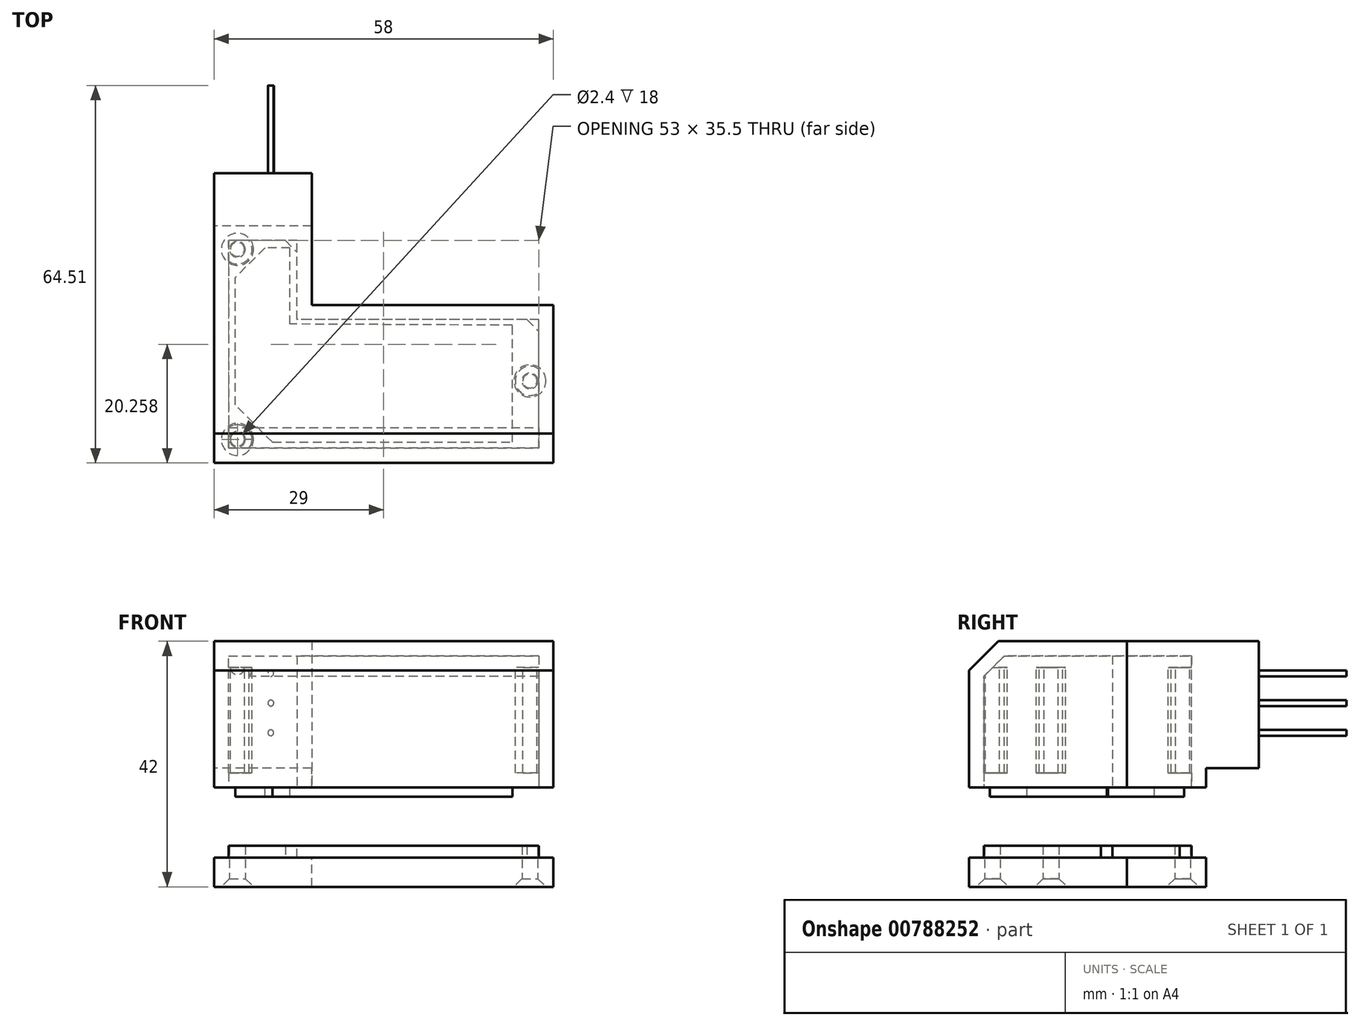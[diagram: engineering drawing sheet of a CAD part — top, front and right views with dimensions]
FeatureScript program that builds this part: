
annotation { "Feature Type Name" : "Feature", "Feature Type Description" : "" }
export const myFeature = defineFeature(function(context is Context, id is Id, definition is map)
    precondition{}
    {
        {
            var Q0;
            Q0=qCreatedBy(makeId("Top.planeOp"),FACE);
            var sketch = newSketch(context, id + "F0", { "sketchPlane" : qUnion([Q0])});
            skLineSegment(sketch, "E0", {"start": v(-27.66, 15.13) * mm, "end": v(-27.66, -18.85) * mm});
            skLineSegment(sketch, "E1", {"start": v(-27.66, -18.85) * mm, "end": v(30.34, -18.85) * mm});
            skLineSegment(sketch, "E2", {"start": v(30.34, -18.85) * mm, "end": v(30.34, 8.15) * mm});
            skLineSegment(sketch, "E3", {"start": v(30.34, 8.15) * mm, "end": v(-10.96, 8.15) * mm});
            skLineSegment(sketch, "E4", {"start": v(-10.96, 8.15) * mm, "end": v(-10.96, 30.65) * mm});
            skLineSegment(sketch, "E5", {"start": v(-10.96, 30.65) * mm, "end": v(-27.66, 30.65) * mm});
            skLineSegment(sketch, "E6", {"start": v(-27.66, 30.65) * mm, "end": v(-27.66, 15.13) * mm});
            skSolve(sketch);
        }
        {
            var Q0;
            Q0=makeQuery(id+"F0.imprint","IMPRINT",FACE,{"disambiguationData":[TD([[makeQuery(id+"F0.imprint","IMPRINT",EDGE,{"derivedFrom":sQuery(id+"F0.wireOp",EDGE,"E0")}),1.0]])]});
            extrude(context, id + "F1", {"entities" : qUnion([Q0]), "depth" : 25 * mm, "offsetDistance" : 25 * mm});
        }
        {
            var Q0;
            Q0=makeQuery(id+"F1.opExtrude","SWEPT_FACE",FACE,{"disambiguationData":[OSD([sQuery(id+"F0.wireOp",EDGE,"E0"),sQuery(id+"F0.wireOp",EDGE,"E6")])]});
            var sketch = newSketch(context, id + "F2", { "sketchPlane" : qUnion([Q0])});
            skLineSegment(sketch, "E7", {"start": v(-30.65, 3.3) * mm, "end": v(-21.65, 3.3) * mm});
            skLineSegment(sketch, "E8", {"start": v(-21.65, 3.3) * mm, "end": v(-21.65, 0) * mm});
            skSolve(sketch);
        }
        {
            var Q0;
            {var subQ0=sQuery(id+"F2.wireOp",EDGE,"E7");Q0=makeQuery(id+"F2.imprint","IMPRINT",FACE,{"disambiguationData":[TD([[makeQuery(id+"F2.imprint","IMPRINT",EDGE,{"derivedFrom":subQ0}),-1.0]])]});}
            var Q1;
            Q1=makeQuery(id+"F1.opExtrude","SWEPT_FACE",FACE,{"disambiguationData":[OSD([sQuery(id+"F0.wireOp",EDGE,"E4")])]});
            extrude(context, id + "F3", {"entities" : qUnion([Q0]), "operationType" : NewBodyOperationType.REMOVE, "endBound" : BoundingType.UP_TO_SURFACE, "oppositeDirection" : true, "depth" : 25 * mm, "endBoundEntityFace" : qUnion([Q1]), "offsetDistance" : 25 * mm});
        }
        {
            var Q0;
            Q0=makeQuery(id+"F1.opExtrude","CAP_EDGE",EDGE,{"disambiguationData":[OSD([sQuery(id+"F0.wireOp",EDGE,"E1")])],"isStart":false});
            chamfer(context, id + "F4", {"entities" : qUnion([Q0]), "width" : 5 * mm, "tangentPropagation" : true});
        }
        {
            var Q0;
            Q0=makeQuery(id+"F1.opExtrude","SWEPT_FACE",FACE,{"disambiguationData":[OSD([sQuery(id+"F0.wireOp",EDGE,"E5")])]});
            var sketch = newSketch(context, id + "F5", { "sketchPlane" : qUnion([Q0])});
            skLineSegment(sketch, "E9", {"start": v(17.96, 25) * mm, "end": v(17.96, 3.3) * mm, "construction": true});
            skCircle(sketch, "E10", {"center": v(17.96, 19.5) * mm, "radius": 0.5 * mm});
            skCircle(sketch, "E11", {"center": v(17.94, 14.42) * mm, "radius": 0.5 * mm});
            skCircle(sketch, "E12", {"center": v(17.96, 9.34) * mm, "radius": 0.5 * mm});
            skSolve(sketch);
        }
        {
            var Q0;
            Q0=makeQuery(id+"F5.imprint","IMPRINT",FACE,{"disambiguationData":[TD([[makeQuery(id+"F5.imprint","IMPRINT",EDGE,{"derivedFrom":sQuery(id+"F5.wireOp",EDGE,"E10")}),1.0]])]});
            var Q1;
            Q1=makeQuery(id+"F5.imprint","IMPRINT",FACE,{"disambiguationData":[TD([[makeQuery(id+"F5.imprint","IMPRINT",EDGE,{"derivedFrom":sQuery(id+"F5.wireOp",EDGE,"E11")}),1.0]])]});
            var Q2;
            Q2=makeQuery(id+"F5.imprint","IMPRINT",FACE,{"disambiguationData":[TD([[makeQuery(id+"F5.imprint","IMPRINT",EDGE,{"derivedFrom":sQuery(id+"F5.wireOp",EDGE,"E12")}),1.0]])]});
            extrude(context, id + "F6", {"entities" : qUnion([Q0, Q1, Q2]), "operationType" : NewBodyOperationType.ADD, "depth" : 15 * mm, "offsetDistance" : 25 * mm});
        }
        {
            var Q0;
            Q0=makeQuery(id+"F1.opExtrude","CAP_FACE",FACE,{"disambiguationData":[OSD([sQuery(id+"F0.wireOp",EDGE,"E0"),sQuery(id+"F0.wireOp",EDGE,"E1"),sQuery(id+"F0.wireOp",EDGE,"E2"),sQuery(id+"F0.wireOp",EDGE,"E3"),sQuery(id+"F0.wireOp",EDGE,"E4"),sQuery(id+"F0.wireOp",EDGE,"E5"),sQuery(id+"F0.wireOp",EDGE,"E6")])],"isStart":true});
            shell(context, id + "F7", {"entities" : qUnion([Q0]), "thickness" : 2.5 * mm});
        }
        {
            var Q0;
            Q0=makeQuery(id+"F7.opShell","OFFSET_FACE",FACE,{"disambiguationData":[OSD([sQuery(id+"F0.wireOp",EDGE,"E5")])]});
            var Q1;
            Q1=makeQuery(id+"F7.opShell","OFFSET_FACE",FACE,{"disambiguationData":[OSD([sQuery(id+"F2.wireOp",EDGE,"E8")])]});
            extrude(context, id + "F8", {"entities" : qUnion([Q0]), "operationType" : NewBodyOperationType.ADD, "endBound" : BoundingType.UP_TO_SURFACE, "depth" : 25 * mm, "endBoundEntityFace" : qUnion([Q1]), "offsetDistance" : 25 * mm});
        }
        {
            var Q0;
            Q0=makeQuery(id+"F1.opExtrude","CAP_FACE",FACE,{"disambiguationData":[OSD([sQuery(id+"F0.wireOp",EDGE,"E0"),sQuery(id+"F0.wireOp",EDGE,"E1"),sQuery(id+"F0.wireOp",EDGE,"E2"),sQuery(id+"F0.wireOp",EDGE,"E3"),sQuery(id+"F0.wireOp",EDGE,"E4"),sQuery(id+"F0.wireOp",EDGE,"E5"),sQuery(id+"F0.wireOp",EDGE,"E6")])],"isStart":true});
            cPlane(context, id + "F9", {"entities" : qUnion([Q0]), "cplaneType" : CPlaneType.OFFSET, "offset" : 10 * mm, "width" : 150 * mm, "height" : 150 * mm});
        }
        {
            var Q0;
            Q0=qCreatedBy(id+"F9.planeOp",FACE);
            var sketch = newSketch(context, id + "F10", { "sketchPlane" : qUnion([Q0])});
            skLineSegment(sketch, "E13", {"start": v(-25.16, 16.35) * mm, "end": v(27.84, 16.35) * mm});
            skLineSegment(sketch, "E14", {"start": v(27.84, 16.35) * mm, "end": v(27.84, -5.65) * mm});
            skLineSegment(sketch, "E15", {"start": v(27.84, -5.65) * mm, "end": v(-13.46, -5.65) * mm});
            skLineSegment(sketch, "E16", {"start": v(-13.46, -5.65) * mm, "end": v(-13.46, -19.15) * mm});
            skLineSegment(sketch, "E17", {"start": v(-13.46, -19.15) * mm, "end": v(-25.16, -19.15) * mm});
            skLineSegment(sketch, "E18", {"start": v(-25.16, 16.35) * mm, "end": v(-25.16, -19.15) * mm});
            skSolve(sketch);
        }
        {
            var Q0;
            {var subQ2=sQuery(id+"F10.wireOp",EDGE,"E13");Q0=makeQuery(id+"F10.imprint","IMPRINT",FACE,{"disambiguationData":[TD([[makeQuery(id+"F10.imprint","IMPRINT",EDGE,{"derivedFrom":subQ2}),-1.0]])]});}
            extrude(context, id + "F11", {"entities" : qUnion([Q0]), "depth" : 2 * mm, "offsetDistance" : 25 * mm});
        }
        {
            var Q0;
            Q0=makeQuery(id+"F11.opExtrude","CAP_FACE",FACE,{"disambiguationData":[OSD([sQuery(id+"F10.wireOp",EDGE,"E13"),sQuery(id+"F10.wireOp",EDGE,"ugxWyxvC-Y8jT-QxUj-v6cB-LJvaZN0y2NzD"),sQuery(id+"F10.wireOp",EDGE,"E14"),sQuery(id+"F10.wireOp",EDGE,"E15"),sQuery(id+"F10.wireOp",EDGE,"E16"),sQuery(id+"F10.wireOp",EDGE,"E17"),sQuery(id+"F10.wireOp",EDGE,"E18")])],"isStart":false});
            var sketch = newSketch(context, id + "F12", { "sketchPlane" : qUnion([Q0])});
            skLineSegment(sketch, "E19", {"start": v(-27.66, -21.65) * mm, "end": v(-10.96, -21.65) * mm});
            skLineSegment(sketch, "E20", {"start": v(-10.96, -21.65) * mm, "end": v(-10.96, -8.15) * mm});
            skLineSegment(sketch, "E21", {"start": v(-10.96, -8.15) * mm, "end": v(30.34, -8.15) * mm});
            skLineSegment(sketch, "E22", {"start": v(30.34, -8.15) * mm, "end": v(30.34, 18.86) * mm});
            skLineSegment(sketch, "E23", {"start": v(30.34, 18.86) * mm, "end": v(28.63, 18.85) * mm});
            skLineSegment(sketch, "E24", {"start": v(28.63, 18.85) * mm, "end": v(-27.66, 18.85) * mm});
            skLineSegment(sketch, "E25", {"start": v(-27.66, 18.85) * mm, "end": v(-27.66, -21.65) * mm});
            skSolve(sketch);
        }
        {
            var Q0;
            Q0=makeQuery(id+"F12.imprint","IMPRINT",FACE,{"disambiguationData":[TD([[makeQuery(id+"F12.imprint","IMPRINT",EDGE,{"derivedFrom":makeQuery(id+"F11.opExtrude","CAP_EDGE",EDGE,{"disambiguationData":[OSD([sQuery(id+"F10.wireOp",EDGE,"E13")])],"isStart":false})}),-1.0]])]});
            var Q1;
            Q1=makeQuery(id+"F12.imprint","IMPRINT",FACE,{"disambiguationData":[TD([[makeQuery(id+"F12.imprint","IMPRINT",EDGE,{"derivedFrom":sQuery(id+"F12.wireOp",EDGE,"E19")}),1.0]])]});
            extrude(context, id + "F13", {"entities" : qUnion([Q0, Q1]), "operationType" : NewBodyOperationType.ADD, "depth" : 5 * mm, "offsetDistance" : 25 * mm});
        }
        {
            var Q0;
            Q0=makeQuery(id+"F13.opExtrude","CAP_FACE",FACE,{"disambiguationData":[OSD([sQuery(id+"F12.wireOp",EDGE,"E19"),sQuery(id+"F12.wireOp",EDGE,"E20"),sQuery(id+"F12.wireOp",EDGE,"E21"),sQuery(id+"F12.wireOp",EDGE,"E22"),sQuery(id+"F12.wireOp",EDGE,"E23"),sQuery(id+"F12.wireOp",EDGE,"E24"),sQuery(id+"F12.wireOp",EDGE,"E25")])],"isStart":false});
            var sketch = newSketch(context, id + "F14", { "sketchPlane" : qUnion([Q0])});
            skPoint(sketch, "E26", {"position": v(-23.66, 14.85) * mm});
            skPoint(sketch, "E27", {"position": v(-23.66, -17.65) * mm});
            skLineSegment(sketch, "E28", {"start": v(-29.6, 4.85) * mm, "end": v(35.29, 4.85) * mm, "construction": true});
            skLineSegment(sketch, "E29", {"start": v(-23.66, 21.05) * mm, "end": v(-23.66, -24.23) * mm, "construction": true});
            skPoint(sketch, "E30", {"position": v(26.34, 4.85) * mm});
            skSolve(sketch);
        }
        {
            var Q0;
            Q0=sQuery(id+"F14.wireOp",VERTEX,"E27");
            var Q1;
            Q1=sQuery(id+"F14.wireOp",VERTEX,"E26");
            var Q2;
            Q2=sQuery(id+"F14.wireOp",VERTEX,"E30");
            var Q3;
            Q3=makeQuery(id+"F1.opExtrude","SWEPT_BODY",BODY,{"disambiguationData":[OSD([sQuery(id+"F0.wireOp",EDGE,"E0"),sQuery(id+"F0.wireOp",EDGE,"E1"),sQuery(id+"F0.wireOp",EDGE,"E2"),sQuery(id+"F0.wireOp",EDGE,"E3"),sQuery(id+"F0.wireOp",EDGE,"E4"),sQuery(id+"F0.wireOp",EDGE,"E5"),sQuery(id+"F0.wireOp",EDGE,"E6")])]});
            var Q4;
            Q4=makeQuery(id+"F11.opExtrude","SWEPT_BODY",BODY,{"disambiguationData":[OSD([sQuery(id+"F10.wireOp",EDGE,"E13"),sQuery(id+"F10.wireOp",EDGE,"ugxWyxvC-Y8jT-QxUj-v6cB-LJvaZN0y2NzD"),sQuery(id+"F10.wireOp",EDGE,"E14"),sQuery(id+"F10.wireOp",EDGE,"E15"),sQuery(id+"F10.wireOp",EDGE,"E16"),sQuery(id+"F10.wireOp",EDGE,"E17"),sQuery(id+"F10.wireOp",EDGE,"E18")])]});
            hole(context, id + "F15", {"style" : HoleStyle.C_SINK, "endStyle" : HoleEndStyle.BLIND, "holeDiameter" : 2.7 * mm, "cSinkDiameter" : 5.5 * mm, "cSinkAngle" : 90 * degree, "majorDiameter" : 5 * mm, "holeDepth" : 7 * mm, "isTappedThrough" : true, "tappedDepth" : 12 * mm, "tapClearance" : 3, "locations" : qUnion([Q0, Q1, Q2]), "scope" : qUnion([Q3, Q4])});
        }
        {
            var Q0;
            Q0=makeQuery(id+"F7.opShell","OFFSET_FACE",FACE,{"disambiguationData":[OSD([sQuery(id+"F0.wireOp",EDGE,"E0"),sQuery(id+"F0.wireOp",EDGE,"E1"),sQuery(id+"F0.wireOp",EDGE,"E2"),sQuery(id+"F0.wireOp",EDGE,"E3"),sQuery(id+"F0.wireOp",EDGE,"E4"),sQuery(id+"F0.wireOp",EDGE,"E5"),sQuery(id+"F0.wireOp",EDGE,"E6")])]});
            var Q1;
            Q1 = qBodyType(qCreatedBy(id + "F17" ,EDGE), BodyType.WIRE);
            cPlane(context, id + "F16", {"entities" : qUnion([Q0, Q1]), "cplaneType" : CPlaneType.OFFSET, "offset" : 2 * mm, "width" : 150 * mm, "height" : 150 * mm});
        }
        {
            var Q0;
            Q0=qCreatedBy(id+"F16.planeOp",FACE);
            var sketch = newSketch(context, id + "F17", { "sketchPlane" : qUnion([Q0])});
            skPoint(sketch, "E31", {"position": v(-23.66, -17.65) * mm});
            skPoint(sketch, "E32", {"position": v(26.34, 4.85) * mm});
            skPoint(sketch, "E33", {"position": v(-23.66, 14.85) * mm});
            skCircle(sketch, "E34", {"center": v(-23.66, 14.85) * mm, "radius": 2.5 * mm});
            skCircle(sketch, "E35", {"center": v(-23.66, -17.65) * mm, "radius": 2.5 * mm});
            skCircle(sketch, "E36", {"center": v(26.34, 4.85) * mm, "radius": 2.5 * mm});
            skCircle(sketch, "E37", {"center": v(-23.66, 14.85) * mm, "radius": 1.2 * mm});
            skCircle(sketch, "E38", {"center": v(-23.66, -17.65) * mm, "radius": 1.2 * mm});
            skCircle(sketch, "E39", {"center": v(26.34, 4.85) * mm, "radius": 1.2 * mm});
            skSolve(sketch);
        }
        {
            var Q0;
            Q0=makeQuery(id+"F17.imprint","IMPRINT",FACE,{"disambiguationData":[TD([[makeQuery(id+"F17.imprint","IMPRINT",EDGE,{"derivedFrom":sQuery(id+"F17.wireOp",EDGE,"E38")}),-1.0]])]});
            var Q1;
            Q1=makeQuery(id+"F17.imprint","IMPRINT",FACE,{"disambiguationData":[TD([[makeQuery(id+"F17.imprint","IMPRINT",EDGE,{"derivedFrom":sQuery(id+"F17.wireOp",EDGE,"E37")}),-1.0]])]});
            var Q2;
            Q2=makeQuery(id+"F17.imprint","IMPRINT",FACE,{"disambiguationData":[TD([[makeQuery(id+"F17.imprint","IMPRINT",EDGE,{"derivedFrom":sQuery(id+"F17.wireOp",EDGE,"E39")}),-1.0]])]});
            var Q3;
            Q3=makeQuery(id+"F1.opExtrude","CAP_FACE",FACE,{"disambiguationData":[OSD([sQuery(id+"F0.wireOp",EDGE,"E0"),sQuery(id+"F0.wireOp",EDGE,"E1"),sQuery(id+"F0.wireOp",EDGE,"E2"),sQuery(id+"F0.wireOp",EDGE,"E3"),sQuery(id+"F0.wireOp",EDGE,"E4"),sQuery(id+"F0.wireOp",EDGE,"E5"),sQuery(id+"F0.wireOp",EDGE,"E6")])],"isStart":true});
            extrude(context, id + "F18", {"entities" : qUnion([Q0, Q1, Q2]), "operationType" : NewBodyOperationType.ADD, "depth" : 18 * mm, "endBoundEntityFace" : qUnion([Q3]), "offsetDistance" : 25 * mm});
        }
        {
            var Q0;
            Q0=makeQuery(id+"F11.opExtrude","SWEPT_EDGE",EDGE,{"disambiguationData":[OSD([sQuery(id+"F10.wireOp",EDGE,"E16"),sQuery(id+"F10.wireOp",EDGE,"E17")])]});
            var Q1;
            Q1=makeQuery(id+"F11.opExtrude","SWEPT_EDGE",EDGE,{"disambiguationData":[OSD([sQuery(id+"F10.wireOp",EDGE,"E14"),sQuery(id+"F10.wireOp",EDGE,"E15")])]});
            chamfer(context, id + "F19", {"entities" : qUnion([Q0, Q1]), "width" : 2 * mm, "tangentPropagation" : true});
        }
        {
            var Q0;
            Q0=makeQuery(id+"F1.opExtrude","CAP_FACE",FACE,{"disambiguationData":[OSD([sQuery(id+"F0.wireOp",EDGE,"E0"),sQuery(id+"F0.wireOp",EDGE,"E1"),sQuery(id+"F0.wireOp",EDGE,"E2"),sQuery(id+"F0.wireOp",EDGE,"E3"),sQuery(id+"F0.wireOp",EDGE,"E4"),sQuery(id+"F0.wireOp",EDGE,"E5"),sQuery(id+"F0.wireOp",EDGE,"E6")])],"isStart":true});
            var sketch = newSketch(context, id + "F20", { "sketchPlane" : qUnion([Q0])});
            skLineSegment(sketch, "E40", {"start": v(-17.66, 15.33) * mm, "end": v(23.34, 15.33) * mm});
            skLineSegment(sketch, "E41", {"start": v(23.34, 15.33) * mm, "end": v(23.34, -4.67) * mm});
            skLineSegment(sketch, "E42", {"start": v(23.34, -4.67) * mm, "end": v(-14.66, -4.86) * mm});
            skLineSegment(sketch, "E43", {"start": v(-14.66, -4.86) * mm, "end": v(-14.66, -17.88) * mm});
            skLineSegment(sketch, "E44", {"start": v(-14.66, -17.88) * mm, "end": v(-18.96, -17.88) * mm});
            skLineSegment(sketch, "E45", {"start": v(-18.96, -17.88) * mm, "end": v(-24, -12.84) * mm});
            skLineSegment(sketch, "E46", {"start": v(-17.66, 15.33) * mm, "end": v(-24, 9) * mm});
            skLineSegment(sketch, "E47", {"start": v(-24, 9) * mm, "end": v(-24, -12.84) * mm});
            skSolve(sketch);
        }
        {
            var Q0;
            Q0=makeQuery(id+"F20.imprint","IMPRINT",FACE,{"disambiguationData":[TD([[makeQuery(id+"F20.imprint","IMPRINT",EDGE,{"derivedFrom":sQuery(id+"F20.wireOp",EDGE,"E40")}),-1.0]])]});
            extrude(context, id + "F21", {"entities" : qUnion([Q0]), "depth" : 1.6 * mm, "offsetDistance" : 25 * mm});
        }
    });
